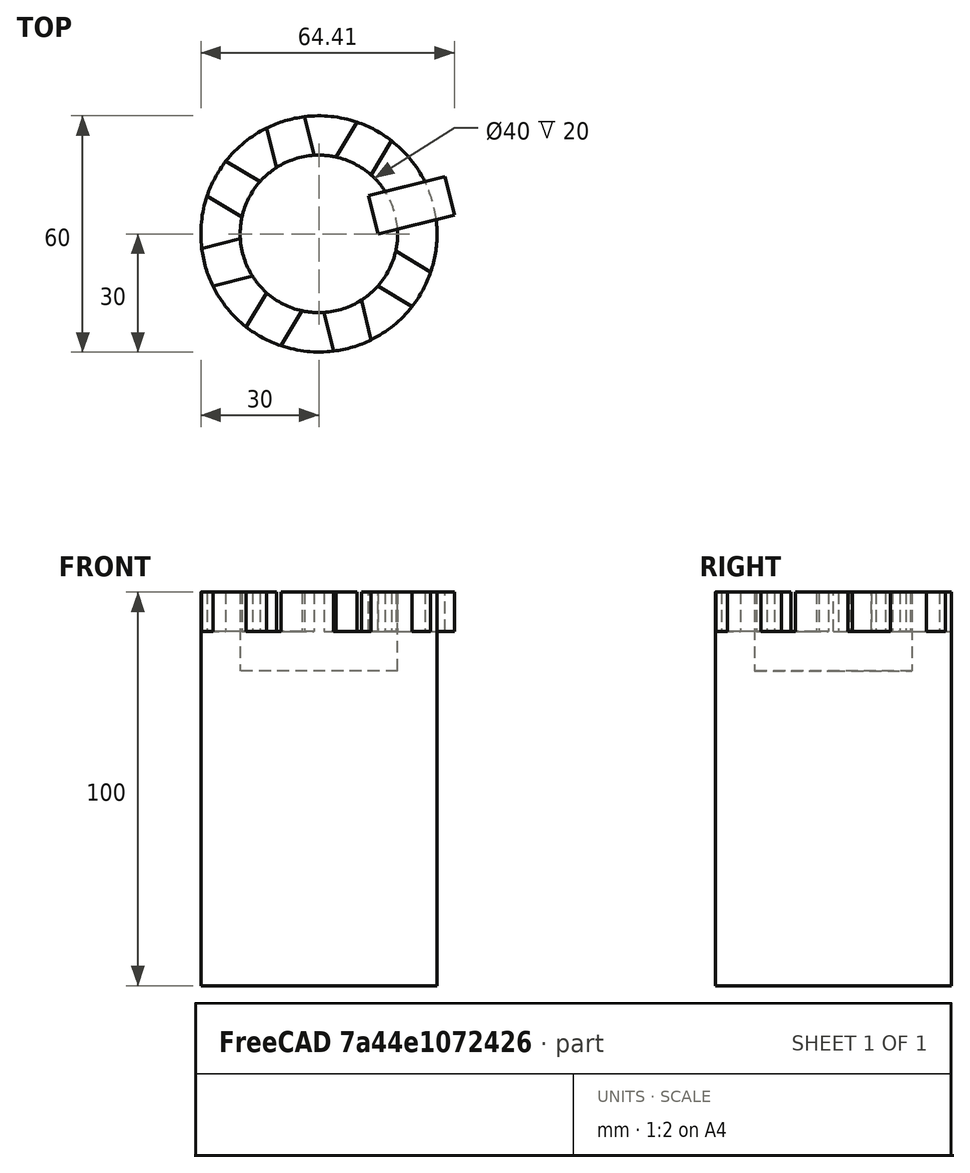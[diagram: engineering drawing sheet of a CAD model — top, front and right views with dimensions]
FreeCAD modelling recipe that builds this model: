
FCSTD DOCUMENT  (FreeCAD 0.21R33771 (Git))
Label: OJT1_T11R03_torre
License: All rights reserved
LicenseURL: http://en.wikipedia.org/wiki/All_rights_reserved
objects: Part::Cylinder×2, Part::Cut×2, Part::Box×1, Part::FeaturePython×1
note: 5 computed .brp shape members not serialized (recipe doc carries the construction recipe); baked Part::Feature solids carry a one-line shape summary decoded from their .brp

FEATURE [Part::Cylinder] Cylinder
  Angle = 360
  AttacherType = Attacher::AttachEngine3D
  FirstAngle = 0
  Height = 100
  Radius = 30
  SecondAngle = 0
FEATURE [Part::Cylinder] Cylinder001
  Angle = 360
  AttacherType = Attacher::AttachEngine3D
  FirstAngle = 0
  Height = 20
  Placement = pos=(0,0,80) rot=(0,0,1;0rad)
  Radius = 20
  SecondAngle = 0
FEATURE [Part::Cut] Cut
  Base = -> Cylinder
  Refine = true
  Tool = -> Cylinder001
FEATURE [Part::Box] Box  label="merlet"
  AttacherType = Attacher::AttachEngine3D
  Height = 10
  Length = 20
  Placement = pos=(15,0,90) rot=(0,0,1;0.244346rad)
  Width = 10
FEATURE [Part::FeaturePython] Array  label="merlets"  # Draft array (typed FeaturePython)
  AlwaysSyncPlacement = false
  Angle = 360
  ArrayType = 1
  Axis = (0,0,1)
  Base = -> Box
  Center = (0,0,1)
  Count = 8
  ExpandArray = false
  Fuse = false
  IntervalAxis = (0,0,0)
  IntervalX = (50,0,0)
  IntervalY = (0,50,0)
  IntervalZ = (0,0,50)
  NumberCircles = 3
  NumberPolar = 8
  NumberX = 2
  NumberY = 2
  NumberZ = 1
  PlacementList = 8 placements: [(15,0,90),(10.6066,10.6066,90),(3.33067e-15,15,90),(-10.6066,10.6066,90),(-15,1.83697e-15,90),(-10.6066,-10.6066,90),(-3.33067e-15,-15,90),(10.6066,-10.6066,90)]
  RadialDistance = 50
  ScaleList = (8) [(1,1,1),(1,1,1),(1,1,1),(1,1,1),(1,1,1),(1,1,1),(1,1,1),(1,1,1)]
  Symmetry = 1
  TangentialDistance = 25
FEATURE [Part::Cut] Cut001  label="torre"
  Base = -> Cut
  Refine = true
  Tool = -> Array
